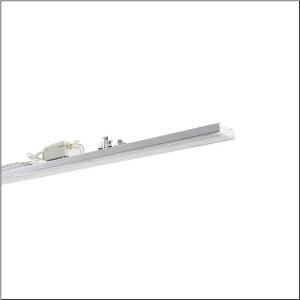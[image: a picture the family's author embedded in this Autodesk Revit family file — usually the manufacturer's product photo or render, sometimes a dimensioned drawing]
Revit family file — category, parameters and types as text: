
# Revit family: licross_r__21_recessed_mo_52tl14cn485g_d932
name_source: partatom
category: Lighting Fixtures
units: mm (PartAtom-declared; Revit-internal decimal feet)

## family parameters
Cut with Voids When Loaded = No
Host = Face
Light Source = No
Part Type = Normal
Room Calculation Point = No
Round Connector Dimension = Use Diameter
Shared = No

## types (1)
- --- (1 x LED, 8530 lm, 49.9 W, 4000K)
    Apparent Load = 50 VA
    CIE Flux Codes = 56 84 97 100 100
    Color Rendering = 80
    Color Temperature = 4000K
    Default Elevation = 1800 mm
    Description = Licross® 21 Recessed MO, luminaire insert, of sheet steel, galvanised, coil coated, white, length: 1.500mm, width: 66mm, height: 67mm, LED rated luminous flux: 8.530lm, light colour: 840, control gear: ON/OFF Multilumen, CLOi, control gear: ECG DALI, with plug, 5-pole, with phase selection, mains connection: 220..240V, AC, 50/60Hz, start of lifetime: 50W, end of service life: 61W, halogen-free wiring, primary light control with lens, of plastic, primary optical cover: cover, of PMMA, light emission: direct distribution, primary light characteristic: asymmetric, protection rating (complete): IP40, insulation class (complete): insulation class I (protective earthing), certification: CE, ENEC, VDE, UKCA, protection symbol: D if used in an environment without relevant dust loads with corresponding accessories, impact resistance: IK06, permissible ambient temperature for indoor applications: -35..+40°C, corresponds to IFS (International Featured Standards) requirements for safety and quality in the food industry, reducing of maximum allowable ambient temperature of 5°C with ceiling mounting, LABS conformity tested according to VDMA 24364:2018-05, packaging unit: 1 piece
    Height = 58 mm
    Lamp = 1 x LED
    Lamp Light Flux = 8530 lm
    Lamp Power = 49.9 W
    Lamp count = 1
    Length = 1500 mm
    Luminous efficacy = 171 lm/W
    Manufacturer = Siteco
    ModVariant = No
    Model = 52TL14CN485G
    Mounting Place = Ceiling
    Mounting Type = Pendant
    Number of Poles = 1
    OnlyDefault = Yes
    Power Factor = 1
    Product Name = Licross® 21 Recessed MO
    Product group = luminaire insert
    ProductGroupID = 901
    Protection Class = Protection class I
    Protection Degree = IP 40
    RLX_Detail_Level = 1
    RLX_Emergency_Light_Flux = 0 lm
    RLX_Emergency_Type = 0
    RLX_Emergency_Type_DB = No
    RlxData = <blob elided: 22745 chars, md5=19f923a8>
    Socket = socket
    Standby Power = 0 W
    System Light Flux = 8530 lm
    System Power = 50 W
    Type Comments = factory setting: luminous flux: 100 % | (A | C | E) | 116 mA
    Type Image = l_1296930.jpg
    URL = http://relux.com
    VarID = @adj_040865
    Voltage = 0 V
    Weight = 0.00 kg
    Width = 66 mm

## geometry (parser evidence)
native form markers: Blend x4, Sweep x11
no freeform markers — native parametric forms only
